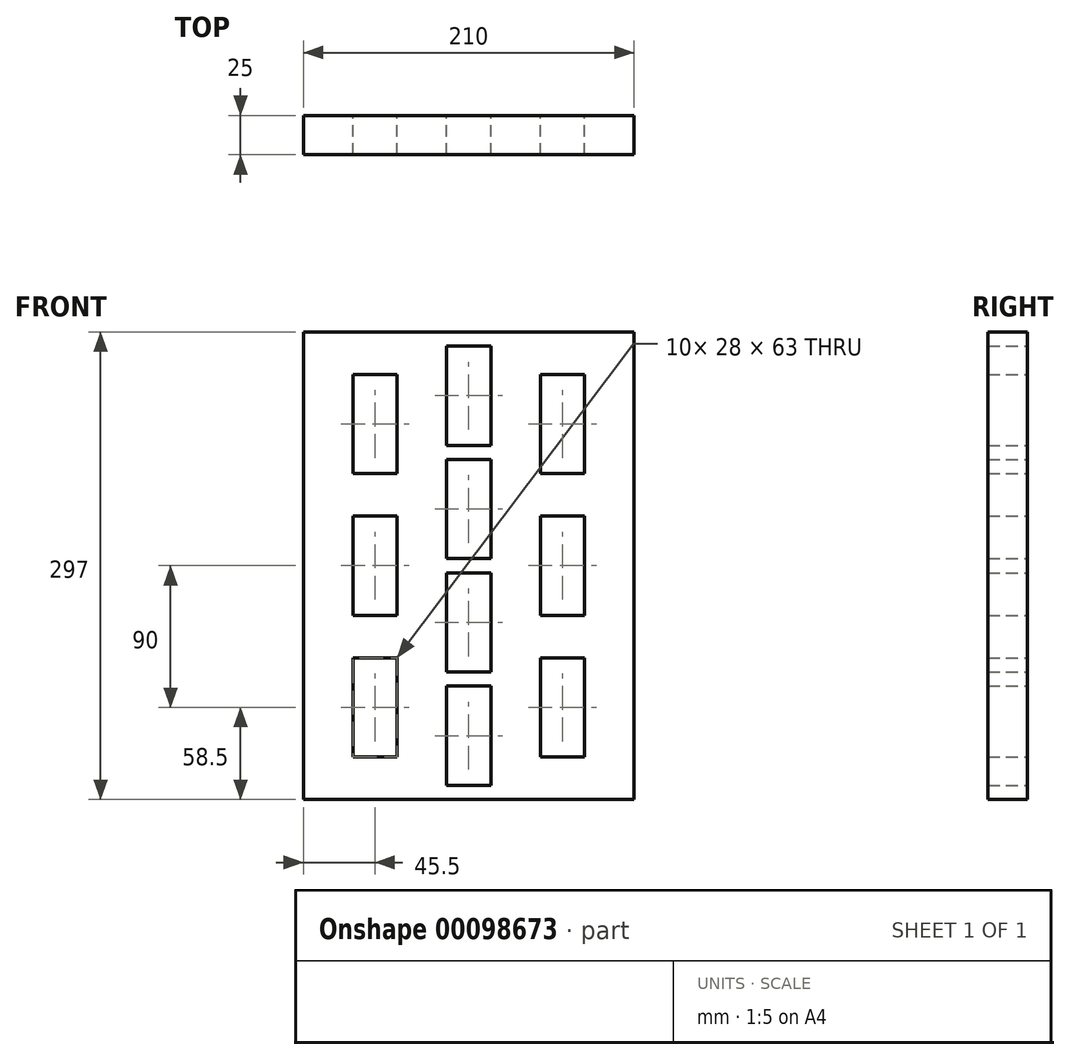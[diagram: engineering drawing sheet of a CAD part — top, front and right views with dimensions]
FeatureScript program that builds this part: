
annotation { "Feature Type Name" : "Feature", "Feature Type Description" : "" }
export const myFeature = defineFeature(function(context is Context, id is Id, definition is map)
    precondition{}
    {
        {
            var Q0;
            Q0=qCreatedBy(makeId("Front.planeOp"),FACE);
            var sketch = newSketch(context, id + "F0", { "sketchPlane" : qUnion([Q0])});
            skLineSegment(sketch, "E0.bottom", {"start": v(105, -148.5) * mm, "end": v(-105, -148.5) * mm});
            skLineSegment(sketch, "E0.top", {"start": v(105, 148.5) * mm, "end": v(-105, 148.5) * mm});
            skLineSegment(sketch, "E0.left", {"start": v(105, -148.5) * mm, "end": v(105, 148.5) * mm});
            skLineSegment(sketch, "E0.right", {"start": v(-105, -148.5) * mm, "end": v(-105, 148.5) * mm});
            skLineSegment(sketch, "E1.bottom", {"start": v(-14, 139.5) * mm, "end": v(14, 139.5) * mm});
            skLineSegment(sketch, "E1.top", {"start": v(-14, 76.5) * mm, "end": v(14, 76.5) * mm});
            skLineSegment(sketch, "E1.left", {"start": v(-14, 139.5) * mm, "end": v(-14, 76.5) * mm});
            skLineSegment(sketch, "E1.right", {"start": v(14, 139.5) * mm, "end": v(14, 76.5) * mm});
            skLineSegment(sketch, "E2.direction1", {"start": v(-14, 76.5) * mm, "end": v(11, 76.5) * mm, "construction": true});
            skLineSegment(sketch, "E3.bottom", {"start": v(-73.5, 121.5) * mm, "end": v(-45.5, 121.5) * mm});
            skLineSegment(sketch, "E3.top", {"start": v(-73.5, 58.5) * mm, "end": v(-45.5, 58.5) * mm});
            skLineSegment(sketch, "E3.left", {"start": v(-73.5, 121.5) * mm, "end": v(-73.5, 58.5) * mm});
            skLineSegment(sketch, "E3.right", {"start": v(-45.5, 121.5) * mm, "end": v(-45.5, 58.5) * mm});
            skLineSegment(sketch, "E4.0.1.0", {"start": v(-73.5, 31.5) * mm, "end": v(-45.5, 31.5) * mm});
            skLineSegment(sketch, "E4.0.1.1", {"start": v(-45.5, 31.5) * mm, "end": v(-45.5, -31.5) * mm});
            skLineSegment(sketch, "E4.0.1.2", {"start": v(-73.5, 31.5) * mm, "end": v(-73.5, -31.5) * mm});
            skLineSegment(sketch, "E4.0.1.3", {"start": v(-73.5, -31.5) * mm, "end": v(-45.5, -31.5) * mm});
            skLineSegment(sketch, "E4.0.2.0", {"start": v(-73.5, -58.5) * mm, "end": v(-45.5, -58.5) * mm});
            skLineSegment(sketch, "E4.0.2.1", {"start": v(-45.5, -58.5) * mm, "end": v(-45.5, -121.5) * mm});
            skLineSegment(sketch, "E4.0.2.2", {"start": v(-73.5, -58.5) * mm, "end": v(-73.5, -121.5) * mm});
            skLineSegment(sketch, "E4.0.2.3", {"start": v(-73.5, -121.5) * mm, "end": v(-45.5, -121.5) * mm});
            skLineSegment(sketch, "E4.direction1", {"start": v(-73.5, 121.5) * mm, "end": v(-48.5, 121.5) * mm, "construction": true});
            skLineSegment(sketch, "E4.direction2", {"start": v(-73.5, 121.5) * mm, "end": v(-73.5, 31.5) * mm, "construction": true});
            skLineSegment(sketch, "E5.MirrorCS", {"start": v(73.5, 121.5) * mm, "end": v(73.5, 58.5) * mm});
            skLineSegment(sketch, "E6.MirrorCS", {"start": v(73.5, 121.5) * mm, "end": v(45.5, 121.5) * mm});
            skLineSegment(sketch, "E7.MirrorCS", {"start": v(73.5, -58.5) * mm, "end": v(45.5, -58.5) * mm});
            skLineSegment(sketch, "E8.MirrorCS", {"start": v(73.5, 121.5) * mm, "end": v(48.5, 121.5) * mm, "construction": true});
            skLineSegment(sketch, "E9.MirrorCS", {"start": v(73.5, 121.5) * mm, "end": v(73.5, 31.5) * mm, "construction": true});
            skLineSegment(sketch, "E10.MirrorCS", {"start": v(73.5, -31.5) * mm, "end": v(45.5, -31.5) * mm});
            skLineSegment(sketch, "E11.MirrorCS", {"start": v(45.5, 31.5) * mm, "end": v(45.5, -31.5) * mm});
            skLineSegment(sketch, "E12.MirrorCS", {"start": v(73.5, -58.5) * mm, "end": v(73.5, -121.5) * mm});
            skLineSegment(sketch, "E13.MirrorCS", {"start": v(45.5, -58.5) * mm, "end": v(45.5, -121.5) * mm});
            skLineSegment(sketch, "E14.MirrorCS", {"start": v(73.5, -121.5) * mm, "end": v(45.5, -121.5) * mm});
            skLineSegment(sketch, "E15.MirrorCS", {"start": v(73.5, 31.5) * mm, "end": v(73.5, -31.5) * mm});
            skLineSegment(sketch, "E16.MirrorCS", {"start": v(73.5, 58.5) * mm, "end": v(45.5, 58.5) * mm});
            skLineSegment(sketch, "E17.MirrorCS", {"start": v(45.5, 121.5) * mm, "end": v(45.5, 58.5) * mm});
            skLineSegment(sketch, "E18.MirrorCS", {"start": v(73.5, 31.5) * mm, "end": v(45.5, 31.5) * mm});
            skLineSegment(sketch, "E19.0.1.0", {"start": v(-14, 67.5) * mm, "end": v(-14, 4.5) * mm});
            skLineSegment(sketch, "E19.0.1.1", {"start": v(-14, 67.5) * mm, "end": v(14, 67.5) * mm});
            skLineSegment(sketch, "E19.0.1.2", {"start": v(14, 67.5) * mm, "end": v(14, 4.5) * mm});
            skLineSegment(sketch, "E19.0.1.3", {"start": v(-14, 4.5) * mm, "end": v(11, 4.5) * mm, "construction": true});
            skLineSegment(sketch, "E19.0.1.4", {"start": v(-14, 4.5) * mm, "end": v(11, 4.5) * mm, "construction": true});
            skLineSegment(sketch, "E19.0.1.5", {"start": v(-14, 4.5) * mm, "end": v(14, 4.5) * mm});
            skLineSegment(sketch, "E19.0.2.0", {"start": v(-14, -4.5) * mm, "end": v(-14, -67.5) * mm});
            skLineSegment(sketch, "E19.0.2.1", {"start": v(-14, -4.5) * mm, "end": v(14, -4.5) * mm});
            skLineSegment(sketch, "E19.0.2.2", {"start": v(14, -4.5) * mm, "end": v(14, -67.5) * mm});
            skLineSegment(sketch, "E19.0.2.3", {"start": v(-14, -67.5) * mm, "end": v(11, -67.5) * mm, "construction": true});
            skLineSegment(sketch, "E19.0.2.4", {"start": v(-14, -67.5) * mm, "end": v(11, -67.5) * mm, "construction": true});
            skLineSegment(sketch, "E19.0.2.5", {"start": v(-14, -67.5) * mm, "end": v(14, -67.5) * mm});
            skLineSegment(sketch, "E19.0.3.0", {"start": v(-14, -76.5) * mm, "end": v(-14, -139.5) * mm});
            skLineSegment(sketch, "E19.0.3.1", {"start": v(-14, -76.5) * mm, "end": v(14, -76.5) * mm});
            skLineSegment(sketch, "E19.0.3.2", {"start": v(14, -76.5) * mm, "end": v(14, -139.5) * mm});
            skLineSegment(sketch, "E19.0.3.3", {"start": v(-14, -139.5) * mm, "end": v(11, -139.5) * mm, "construction": true});
            skLineSegment(sketch, "E19.0.3.4", {"start": v(-14, -139.5) * mm, "end": v(11, -139.5) * mm, "construction": true});
            skLineSegment(sketch, "E19.0.3.5", {"start": v(-14, -139.5) * mm, "end": v(14, -139.5) * mm});
            skLineSegment(sketch, "E19.direction2", {"start": v(-14, 76.5) * mm, "end": v(-14, 4.5) * mm, "construction": true});
            skSolve(sketch);
        }
        {
            var Q0;
            Q0 = qSketchRegion(id + "F0", true);
            extrude(context, id + "F1", {"entities" : qUnion([Q0]), "depth" : 25 * mm});
        }
    });
